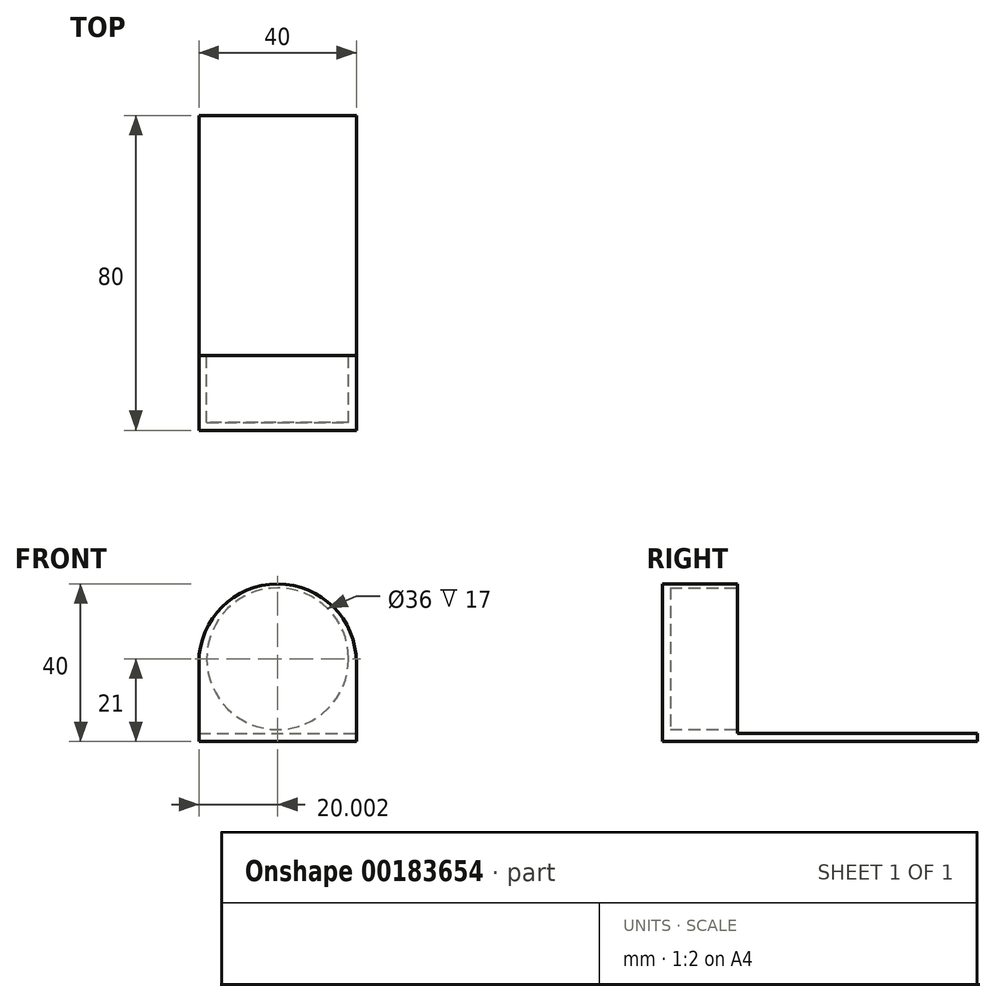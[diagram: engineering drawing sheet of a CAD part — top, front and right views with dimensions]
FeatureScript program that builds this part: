
annotation { "Feature Type Name" : "Feature", "Feature Type Description" : "" }
export const myFeature = defineFeature(function(context is Context, id is Id, definition is map)
    precondition{}
    {
        {
            var Q0;
            Q0=qCreatedBy(makeId("Top.planeOp"),FACE);
            var sketch = newSketch(context, id + "F0", { "sketchPlane" : qUnion([Q0])});
            skLineSegment(sketch, "E0.bottom", {"start": v(-22.85, 59.12) * mm, "end": v(17.15, 59.12) * mm});
            skLineSegment(sketch, "E0.top", {"start": v(-22.85, -20.88) * mm, "end": v(17.15, -20.88) * mm});
            skLineSegment(sketch, "E0.left", {"start": v(-22.85, 59.12) * mm, "end": v(-22.85, -20.88) * mm});
            skLineSegment(sketch, "E0.right", {"start": v(17.15, 59.12) * mm, "end": v(17.15, -20.88) * mm});
            skLineSegment(sketch, "E1", {"start": v(-22.85, -1.88) * mm, "end": v(17.15, -1.88) * mm});
            skSolve(sketch);
        }
        {
            var Q0;
            {var subQ0=sQuery(id+"F0.wireOp",EDGE,"E0.bottom");Q0=makeQuery(id+"F0.imprint","IMPRINT",FACE,{"disambiguationData":[TD([[makeQuery(id+"F0.imprint","IMPRINT",EDGE,{"derivedFrom":subQ0}),-1.0]])]});}
            extrude(context, id + "F1", {"entities" : qUnion([Q0]), "depth" : 2 * mm});
        }
        {
            var Q0;
            {var subQ0=sQuery(id+"F0.wireOp",EDGE,"E0.top");Q0=makeQuery(id+"F0.imprint","IMPRINT",FACE,{"disambiguationData":[TD([[makeQuery(id+"F0.imprint","IMPRINT",EDGE,{"derivedFrom":subQ0}),1.0]])]});}
            extrude(context, id + "F2", {"entities" : qUnion([Q0]), "operationType" : NewBodyOperationType.ADD, "depth" : 40 * mm});
        }
        {
            var Q0;
            Q0=makeQuery(id+"F2.opExtrude","SWEPT_FACE",FACE,{"disambiguationData":[OSD([sQuery(id+"F0.wireOp",EDGE,"E1")])]});
            var sketch = newSketch(context, id + "F3", { "sketchPlane" : qUnion([Q0])});
            skCircle(sketch, "E2", {"center": v(2.85, 21) * mm, "radius": 18 * mm});
            skPoint(sketch, "E2.centerSnap0", {"position": v(2.85, 40) * mm});
            skPoint(sketch, "E2.centerSnap1", {"position": v(22.85, 21) * mm});
            skSolve(sketch);
        }
        {
            var Q0;
            Q0=qSketchRegion(id+"F3",true);
            extrude(context, id + "F4", {"entities" : qUnion([Q0]), "operationType" : NewBodyOperationType.REMOVE, "oppositeDirection" : true, "depth" : 17 * mm});
        }
        {
            var Q0;
            Q0=makeQuery(id+"F2.opExtrude","CAP_EDGE",EDGE,{"disambiguationData":[OSD([sQuery(id+"F0.wireOp",EDGE,"E0.right")])],"isStart":false});
            var Q1;
            Q1=makeQuery(id+"F2.opExtrude","CAP_EDGE",EDGE,{"disambiguationData":[OSD([sQuery(id+"F0.wireOp",EDGE,"E0.left")])],"isStart":false});
            fillet(context, id + "F5", {"entities" : qUnion([Q0, Q1]), "radius" : 20 * mm, "tangentPropagation" : true, "allowEdgeOverflow" : false});
        }
    });
